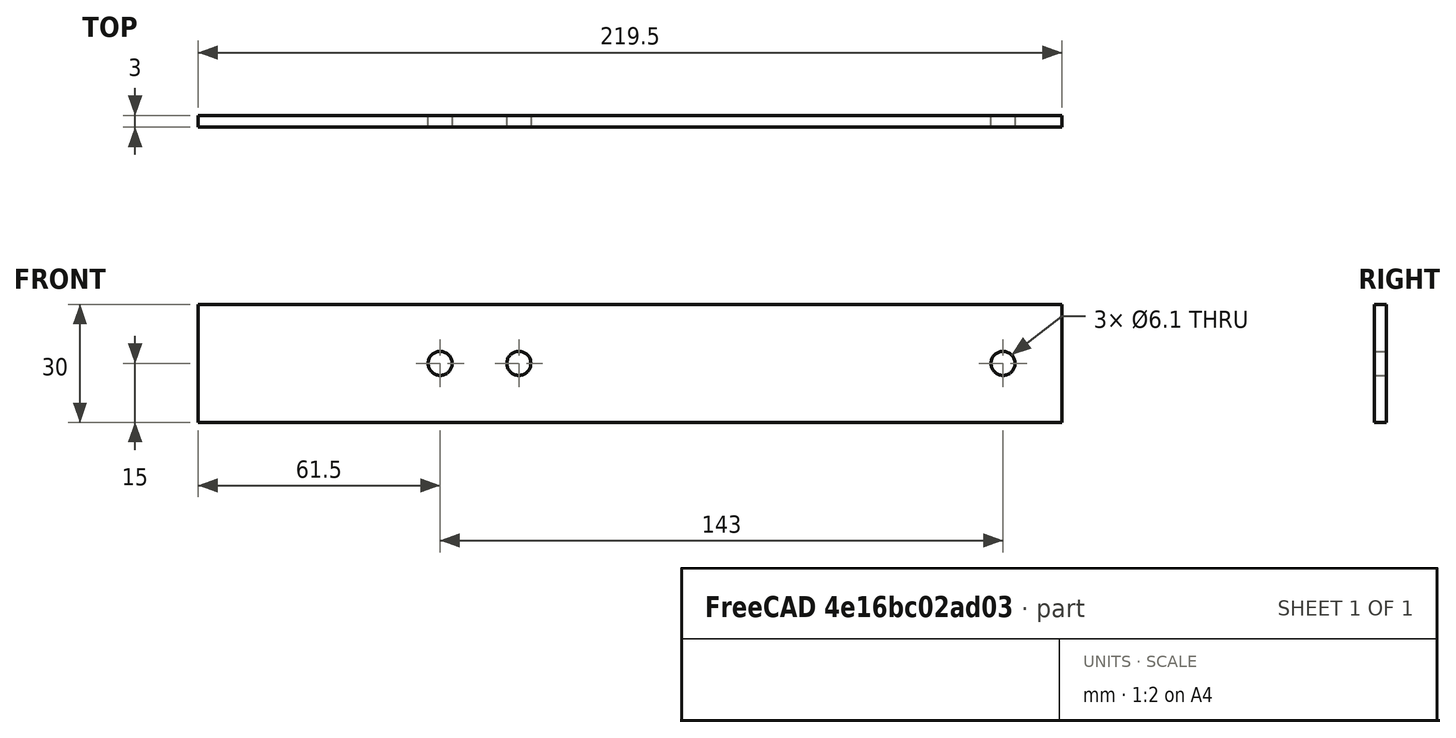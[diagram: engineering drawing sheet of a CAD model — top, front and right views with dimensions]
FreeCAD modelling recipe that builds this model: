
FCSTD DOCUMENT  (FreeCAD 0.15R4671 (Git))
Label: gabarit théorique
License: All rights reserved
LicenseURL: http://en.wikipedia.org/wiki/All_rights_reserved
objects: Sketcher::SketchObject×1, PartDesign::Pad×1
note: 3 computed .brp shape members not serialized (recipe doc carries the construction recipe); baked Part::Feature solids carry a one-line shape summary decoded from their .brp

FEATURE [Sketcher::SketchObject] Sketch
  Placement = pos=(0,0,0) rot=(-1,0,0;4.71239rad)
  sketch-geometry (7):
    g0: Circle CenterX=-10 CenterY=0 CenterZ=0 NormalX=0 NormalY=0 NormalZ=1 Radius=3.05
    g1: Circle CenterX=10 CenterY=0 CenterZ=0 NormalX=0 NormalY=0 NormalZ=1 Radius=3.05
    g2: LineSegment StartX=-71.5 StartY=15 StartZ=0 EndX=148 EndY=15 EndZ=0
    g3: LineSegment StartX=148 StartY=15 StartZ=0 EndX=148 EndY=-15 EndZ=0
    g4: LineSegment StartX=148 StartY=-15 StartZ=0 EndX=-71.5 EndY=-15 EndZ=0
    g5: LineSegment StartX=-71.5 StartY=-15 StartZ=0 EndX=-71.5 EndY=15 EndZ=0
    g6: Circle CenterX=133 CenterY=0 CenterZ=0 NormalX=0 NormalY=0 NormalZ=1 Radius=3.05
  constraints (21):
    c: PointOnObject(g0,g-1)
    c: PointOnObject(g1,g-1)
    c: Symmetric(g0,g1,g-2)
    c: DistanceX(g0,g1) = 20
    c: Coincident(g2,g3)
    c: Coincident(g3,g4)
    c: Coincident(g4,g5)
    c: Coincident(g5,g2)
    c: Horizontal(g2)
    c: Horizontal(g4)
    c: Vertical(g3)
    c: Vertical(g5)
    c: DistanceY(g5) = 30
    c: Symmetric(g2,g4,g-1)
    c: PointOnObject(g6,g-1)
    c: Radius(g0) = 3.05
    c: Equal(g0,g1)
    c: Equal(g0,g6)
    c: DistanceX(g0,g6) = 143
    c: DistanceX(g6,g3) = 15
    c: DistanceX(g2,g0) = 61.5
FEATURE [PartDesign::Pad] Pad
  Length = 3
  Length2 = 100
  Placement = pos=(0,0,0) rot=(-1,0,0;4.71239rad)
  Sketch = -> Sketch
  Type = 0
